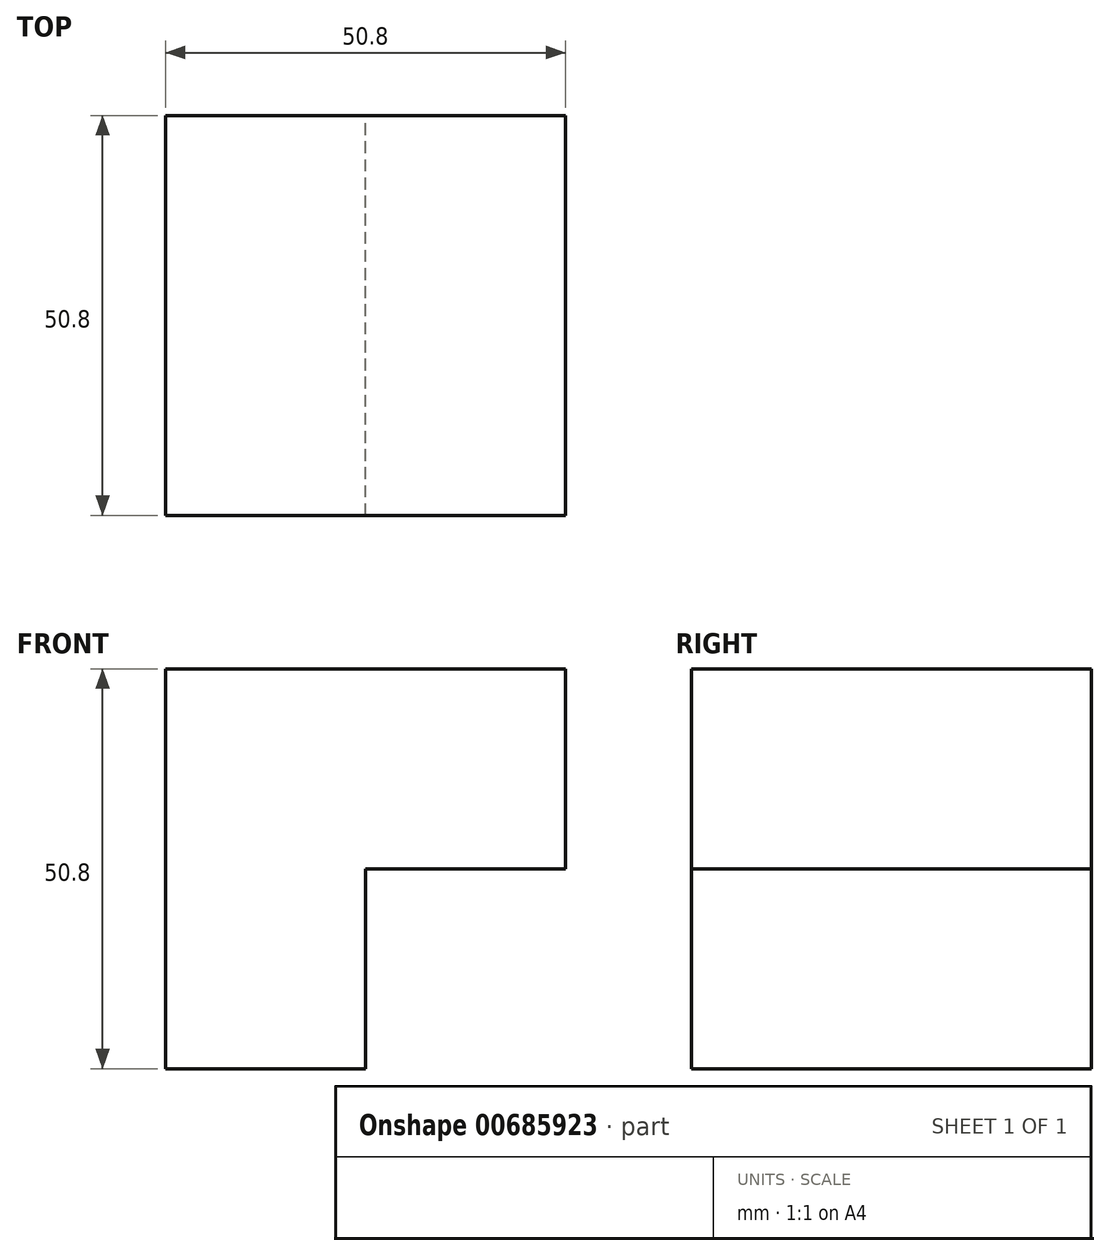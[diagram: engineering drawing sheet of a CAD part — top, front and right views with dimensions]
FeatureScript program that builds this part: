
annotation { "Feature Type Name" : "Feature", "Feature Type Description" : "" }
export const myFeature = defineFeature(function(context is Context, id is Id, definition is map)
    precondition{}
    {
        {
            var Q0;
            Q0=qCreatedBy(makeId("Front.planeOp"),FACE);
            var sketch = newSketch(context, id + "F0", { "sketchPlane" : qUnion([Q0])});
            skLineSegment(sketch, "E0", {"start": v(0, 0) * mm, "end": v(0, 50.8) * mm});
            skLineSegment(sketch, "E1", {"start": v(0, 50.8) * mm, "end": v(50.8, 50.8) * mm});
            skLineSegment(sketch, "E2", {"start": v(0, 0) * mm, "end": v(25.4, 0) * mm});
            skLineSegment(sketch, "E3", {"start": v(25.4, 0) * mm, "end": v(25.4, 25.4) * mm});
            skLineSegment(sketch, "E4", {"start": v(25.4, 25.4) * mm, "end": v(50.8, 25.4) * mm});
            skLineSegment(sketch, "E5", {"start": v(50.8, 25.4) * mm, "end": v(50.8, 50.8) * mm});
            skSolve(sketch);
        }
        {
            var Q0;
            Q0=makeQuery(id+"F0.imprint","IMPRINT",FACE,{"disambiguationData":[TD([[makeQuery(id+"F0.imprint","IMPRINT",EDGE,{"derivedFrom":sQuery(id+"F0.wireOp",EDGE,"E0")}),-1.0]])]});
            extrude(context, id + "F1", {"entities" : qUnion([Q0]), "depth" : 25.4 * mm, "offsetDistance" : 25.4 * mm});
        }
        {
            var Q0;
            Q0=makeQuery(id+"F1.opExtrude","CAP_FACE",FACE,{"disambiguationData":[OSD([sQuery(id+"F0.wireOp",EDGE,"E0"),sQuery(id+"F0.wireOp",EDGE,"E1"),sQuery(id+"F0.wireOp",EDGE,"E2"),sQuery(id+"F0.wireOp",EDGE,"E3"),sQuery(id+"F0.wireOp",EDGE,"E4"),sQuery(id+"F0.wireOp",EDGE,"E5")])],"isStart":false});
            var Q1;
            Q1 = qSketchRegion(id + "F0", true);
            extrude(context, id + "F2", {"entities" : qUnion([Q0, Q1]), "operationType" : NewBodyOperationType.ADD, "depth" : 25.4 * mm, "offsetDistance" : 25.4 * mm});
        }
    });
